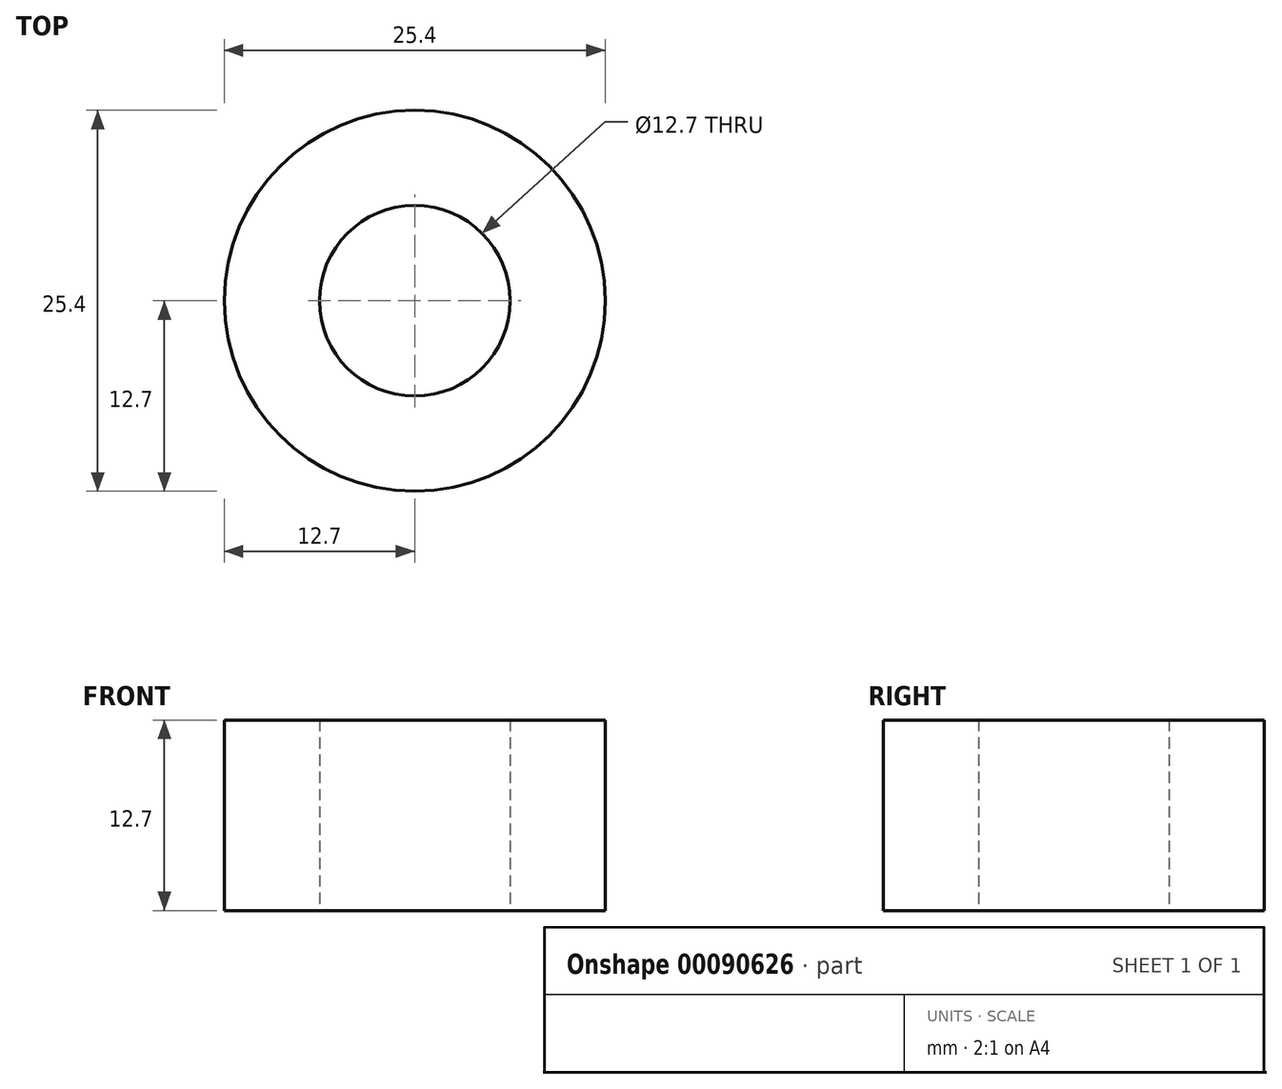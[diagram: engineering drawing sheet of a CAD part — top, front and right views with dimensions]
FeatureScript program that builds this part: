
annotation { "Feature Type Name" : "Feature", "Feature Type Description" : "" }
export const myFeature = defineFeature(function(context is Context, id is Id, definition is map)
    precondition{}
    {
        {
            var Q0;
            Q0=qCreatedBy(makeId("Top.planeOp"),FACE);
            var sketch = newSketch(context, id + "F0", { "sketchPlane" : qUnion([Q0])});
            skCircle(sketch, "E0", {"center": v(0, 0) * mm, "radius": 6.35 * mm});
            skCircle(sketch, "E1", {"center": v(0, 0) * mm, "radius": 12.7 * mm});
            skSolve(sketch);
        }
        {
            var Q0;
            Q0=makeQuery(id+"F0.imprint","IMPRINT",FACE,{"disambiguationData":[TD([[makeQuery(id+"F0.imprint","IMPRINT",EDGE,{"derivedFrom":sQuery(id+"F0.wireOp",EDGE,"E0")}),-1.0]])]});
            extrude(context, id + "F1", {"entities" : qUnion([Q0]), "depth" : 12.7 * mm});
        }
    });
